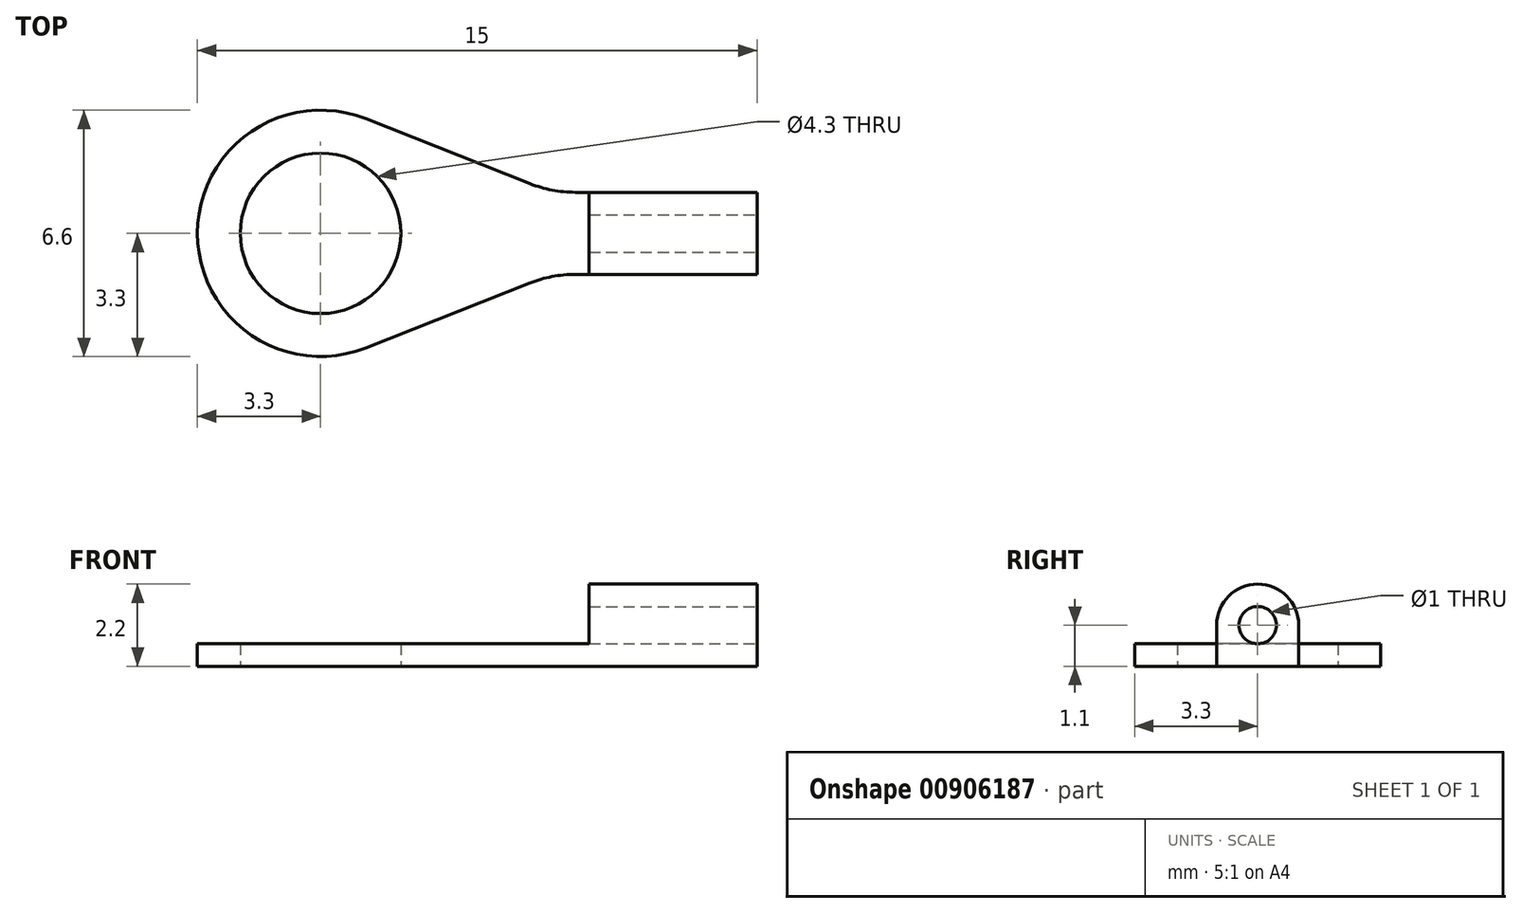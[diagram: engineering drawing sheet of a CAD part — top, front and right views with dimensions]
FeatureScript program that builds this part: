
annotation { "Feature Type Name" : "Feature", "Feature Type Description" : "" }
export const myFeature = defineFeature(function(context is Context, id is Id, definition is map)
    precondition{}
    {
        {
            var Q0;
            Q0=qCreatedBy(makeId("Top.planeOp"),FACE);
            var sketch = newSketch(context, id + "F0", { "sketchPlane" : qUnion([Q0])});
            skLineSegment(sketch, "E0", {"start": v(15, 2.2) * mm, "end": v(15, 4.4) * mm});
            skLineSegment(sketch, "E1", {"start": v(0, 3.3) * mm, "end": v(0, 3.3) * mm});
            skPoint(sketch, "E2.visualSharp", {"position": v(0, 6.6) * mm});
            skArc(sketch, "E2.filletArc", {"start": v(3.3, 6.6) * mm, "mid": v(0.97, 5.63) * mm, "end": v(0, 3.3) * mm});
            skPoint(sketch, "E3.visualSharp", {"position": v(0, 0) * mm});
            skArc(sketch, "E3.filletArc", {"start": v(0, 3.3) * mm, "mid": v(0.97, 0.97) * mm, "end": v(3.3, 0) * mm});
            skLineSegment(sketch, "E4.0", {"start": v(10.5, 2.2) * mm, "end": v(10.5, 4.4) * mm});
            skLineSegment(sketch, "E5.0", {"start": v(9.5, 2.14) * mm, "end": v(9.5, 4.46) * mm});
            skLineSegment(sketch, "E6.0", {"start": v(3.3, 0) * mm, "end": v(3.3, 6.6) * mm});
            skCircle(sketch, "E7", {"center": v(3.3, 3.3) * mm, "radius": 2.15 * mm});
            skLineSegment(sketch, "E8.0", {"start": v(15, 4.4) * mm, "end": v(10.13, 4.4) * mm});
            skLineSegment(sketch, "E9.0", {"start": v(15, 2.2) * mm, "end": v(10.13, 2.2) * mm});
            skArc(sketch, "E10", {"start": v(4.51, 6.37) * mm, "mid": v(0, 3.3) * mm, "end": v(4.51, 0.23) * mm});
            skLineSegment(sketch, "E11", {"start": v(8.92, 4.63) * mm, "end": v(4.51, 6.37) * mm});
            skLineSegment(sketch, "E12", {"start": v(8.92, 1.97) * mm, "end": v(4.51, 0.23) * mm});
            skPoint(sketch, "E13.visualSharp", {"position": v(9.5, 4.4) * mm});
            skArc(sketch, "E13.filletArc", {"start": v(8.92, 4.63) * mm, "mid": v(9.51, 4.46) * mm, "end": v(10.13, 4.4) * mm});
            skPoint(sketch, "E14.visualSharp", {"position": v(9.5, 2.2) * mm});
            skArc(sketch, "E14.filletArc", {"start": v(10.13, 2.2) * mm, "mid": v(9.51, 2.14) * mm, "end": v(8.92, 1.97) * mm});
            skPoint(sketch, "E15.orphan", {"position": v(15, 3.3) * mm});
            skPoint(sketch, "E16.end.orphan", {"position": v(9.5, 3.3) * mm});
            skPoint(sketch, "E17.orphan", {"position": v(15, 6.6) * mm});
            skPoint(sketch, "E18.start.orphan", {"position": v(9.5, 6.6) * mm});
            skPoint(sketch, "E19.orphan", {"position": v(15, 0) * mm});
            skPoint(sketch, "E20.end.orphan", {"position": v(9.5, 0) * mm});
            skSolve(sketch);
        }
        {
            var Q0;
            {var subQ8=sQuery(id+"F0.wireOp",EDGE,"E5.0");Q0=makeQuery(id+"F0.imprint","IMPRINT",FACE,{"disambiguationData":[TD([[makeQuery(id+"F0.imprint","IMPRINT",EDGE,{"derivedFrom":subQ8}),1.0]])]});}
            var Q1;
            Q1 = qSketchRegion(id + "F0", true);
            extrude(context, id + "F1", {"entities" : qUnion([Q0, Q1]), "depth" : 0.6 * mm, "offsetDistance" : 25 * mm});
        }
        {
            var Q0;
            Q0=makeQuery(id+"F1.opExtrude","CAP_FACE",FACE,{"disambiguationData":[OSD([sQuery(id+"F0.wireOp",EDGE,"E0"),sQuery(id+"F0.wireOp",EDGE,"E7"),sQuery(id+"F0.wireOp",EDGE,"E8.0"),sQuery(id+"F0.wireOp",EDGE,"E9.0"),sQuery(id+"F0.wireOp",EDGE,"E10"),sQuery(id+"F0.wireOp",EDGE,"E11"),sQuery(id+"F0.wireOp",EDGE,"E12"),sQuery(id+"F0.wireOp",EDGE,"E13.filletArc"),sQuery(id+"F0.wireOp",EDGE,"E14.filletArc")])],"isStart":false});
            var sketch = newSketch(context, id + "F2", { "sketchPlane" : qUnion([Q0])});
            skLineSegment(sketch, "E21.bottom", {"start": v(15, 4.4) * mm, "end": v(10.5, 4.4) * mm});
            skLineSegment(sketch, "E21.top", {"start": v(15, 2.2) * mm, "end": v(10.5, 2.2) * mm});
            skLineSegment(sketch, "E21.left", {"start": v(15, 4.4) * mm, "end": v(15, 2.2) * mm});
            skLineSegment(sketch, "E21.right", {"start": v(10.5, 4.4) * mm, "end": v(10.5, 2.2) * mm});
            skSolve(sketch);
        }
        {
            var Q0;
            Q0=makeQuery(id+"F2.imprint","IMPRINT",FACE,{"disambiguationData":[TD([[makeQuery(id+"F2.imprint","IMPRINT",EDGE,{"derivedFrom":sQuery(id+"F2.wireOp",EDGE,"E21.bottom")}),1.0]])]});
            extrude(context, id + "F3", {"entities" : qUnion([Q0]), "operationType" : NewBodyOperationType.ADD, "depth" : 1.6 * mm, "offsetDistance" : 25 * mm});
        }
        {
            var Q0;
            Q0=makeQuery(id+"F3.opExtrude","CAP_EDGE",EDGE,{"disambiguationData":[OSD([sQuery(id+"F2.wireOp",EDGE,"E21.bottom")])],"isStart":false});
            var Q1;
            Q1=makeQuery(id+"F3.opExtrude","CAP_EDGE",EDGE,{"disambiguationData":[OSD([sQuery(id+"F2.wireOp",EDGE,"E21.top")])],"isStart":false});
            fillet(context, id + "F4", {"entities" : qUnion([Q0, Q1]), "radius" : 1.1 * mm, "tangentPropagation" : true, "allowEdgeOverflow" : false});
        }
        {
            var Q0;
            Q0=makeQuery(id+"F3.boolean.opBoolean","MERGE",FACE,{"derivedFrom":[makeQuery(id+"F1.opExtrude","SWEPT_FACE",FACE,{"disambiguationData":[OSD([sQuery(id+"F0.wireOp",EDGE,"E0")])]}),makeQuery(id+"F3.opExtrude","SWEPT_FACE",FACE,{"disambiguationData":[OSD([sQuery(id+"F2.wireOp",EDGE,"E21.left")])]})]});
            var sketch = newSketch(context, id + "F5", { "sketchPlane" : qUnion([Q0])});
            skCircle(sketch, "E22", {"center": v(3.3, 1.1) * mm, "radius": 0.5 * mm});
            skSolve(sketch);
        }
        {
            var Q0;
            Q0=makeQuery(id+"F5.imprint","IMPRINT",FACE,{"disambiguationData":[TD([[makeQuery(id+"F5.imprint","IMPRINT",EDGE,{"derivedFrom":sQuery(id+"F5.wireOp",EDGE,"E22")}),1.0]])]});
            extrude(context, id + "F6", {"entities" : qUnion([Q0]), "operationType" : NewBodyOperationType.REMOVE, "oppositeDirection" : true, "depth" : 25 * mm, "offsetDistance" : 25 * mm});
        }
    });
